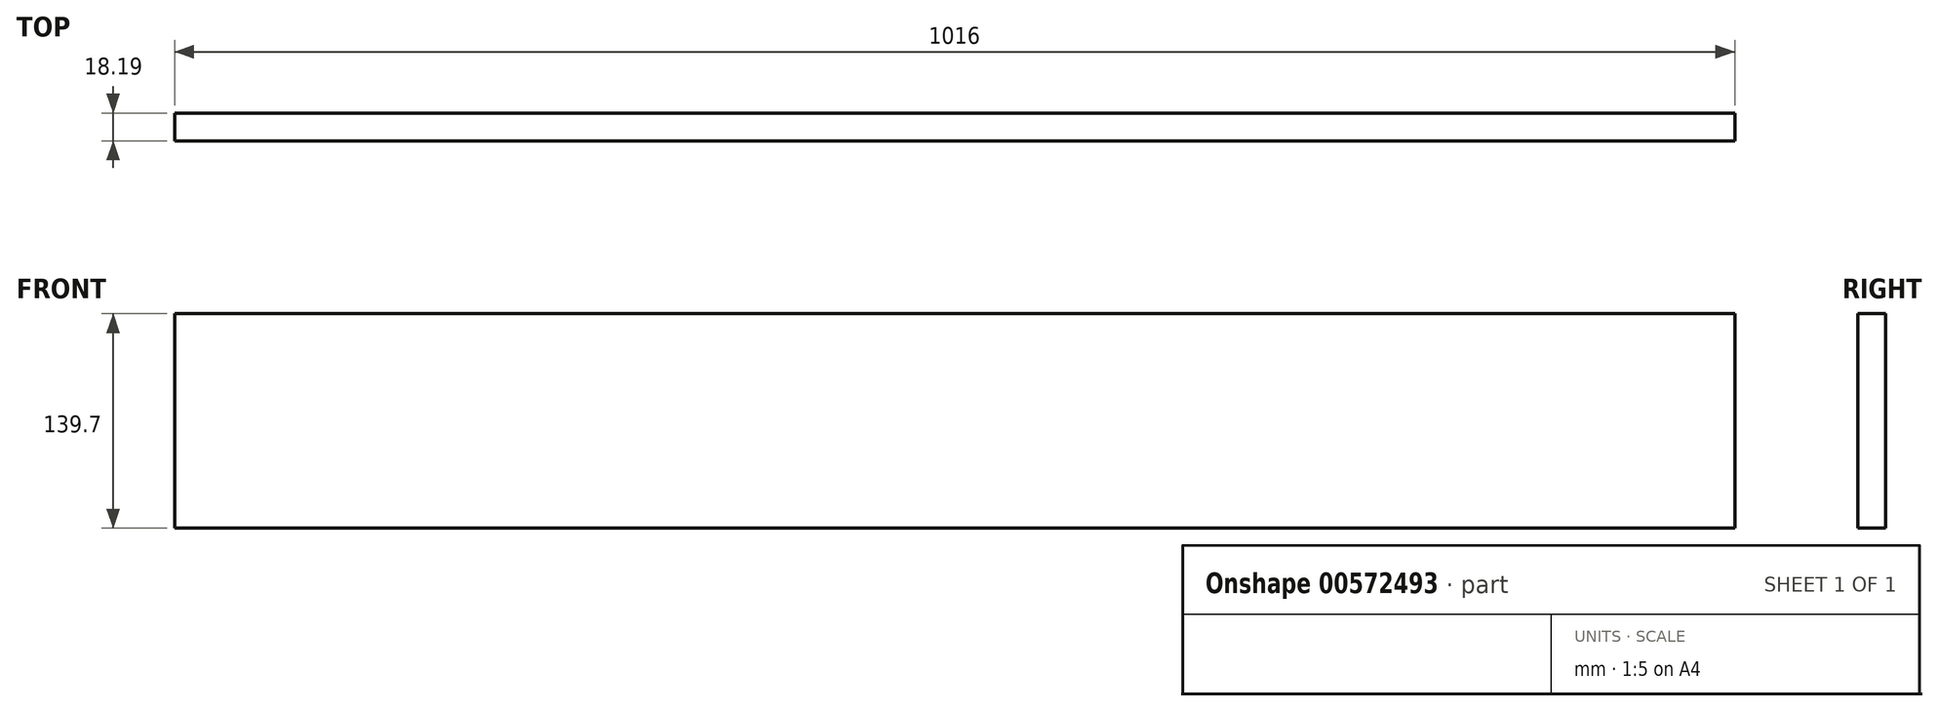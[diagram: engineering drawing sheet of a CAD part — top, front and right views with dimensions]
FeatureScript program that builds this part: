
annotation { "Feature Type Name" : "Feature", "Feature Type Description" : "" }
export const myFeature = defineFeature(function(context is Context, id is Id, definition is map)
    precondition{}
    {
        {
            var Q0;
            Q0=qCreatedBy(makeId("Front.planeOp"),FACE);
            var sketch = newSketch(context, id + "F0", { "sketchPlane" : qUnion([Q0])});
            skLineSegment(sketch, "E0.bottom", {"start": v(-67.64, 77.24) * mm, "end": v(948.36, 77.24) * mm});
            skLineSegment(sketch, "E0.top", {"start": v(-67.64, -62.46) * mm, "end": v(948.36, -62.46) * mm});
            skLineSegment(sketch, "E0.left", {"start": v(-67.64, 77.24) * mm, "end": v(-67.64, -62.46) * mm});
            skLineSegment(sketch, "E0.right", {"start": v(948.36, 77.24) * mm, "end": v(948.36, -62.46) * mm});
            skSolve(sketch);
        }
        {
            var Q0;
            Q0 = qSketchRegion(id + "F0", true);
            extrude(context, id + "F1", {"entities" : qUnion([Q0]), "depth" : 18.2 * mm, "offsetDistance" : 25.4 * mm});
        }
    });
